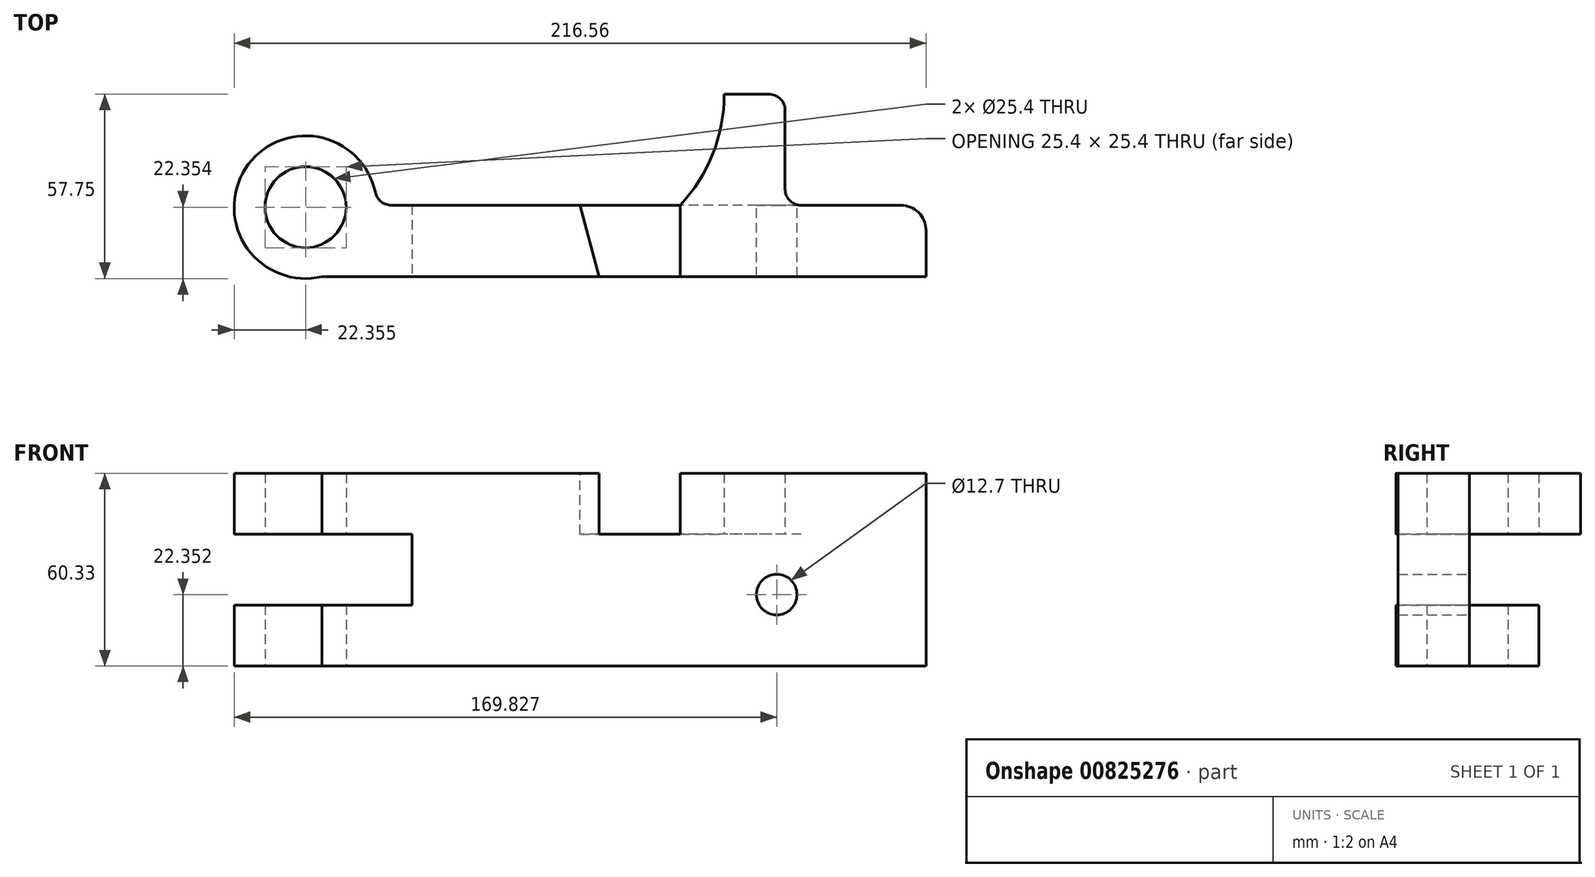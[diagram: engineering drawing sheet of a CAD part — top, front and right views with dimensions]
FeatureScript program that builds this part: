
annotation { "Feature Type Name" : "Feature", "Feature Type Description" : "" }
export const myFeature = defineFeature(function(context is Context, id is Id, definition is map)
    precondition{}
    {
        {
            var Q0;
            Q0=qCreatedBy(makeId("Top.planeOp"),FACE);
            var sketch = newSketch(context, id + "F0", { "sketchPlane" : qUnion([Q0])});
            skLineSegment(sketch, "E0", {"start": v(-131.04, -67.31) * mm, "end": v(58.03, -67.31) * mm});
            skArc(sketch, "E1", {"start": v(-113.83, -44.96) * mm, "mid": v(-153.89, -31.92) * mm, "end": v(-131.04, -67.31) * mm});
            skCircle(sketch, "E2", {"center": v(-136.18, -45.56) * mm, "radius": 12.7 * mm});
            skLineSegment(sketch, "E3", {"start": v(-18.93, -67.31) * mm, "end": v(-44.33, -67.31) * mm});
            skLineSegment(sketch, "E4", {"start": v(-113.83, -44.96) * mm, "end": v(58.03, -44.96) * mm});
            skLineSegment(sketch, "E5", {"start": v(58.03, -44.96) * mm, "end": v(58.03, -67.31) * mm});
            skLineSegment(sketch, "E6", {"start": v(-44.33, -67.31) * mm, "end": v(-50.32, -44.96) * mm});
            skLineSegment(sketch, "E7", {"start": v(-50.32, -44.96) * mm, "end": v(-18.93, -44.96) * mm});
            skLineSegment(sketch, "E8", {"start": v(-18.93, -44.96) * mm, "end": v(-18.93, -67.31) * mm});
            skLineSegment(sketch, "E9", {"start": v(13.91, -44.96) * mm, "end": v(13.91, -10.16) * mm});
            skLineSegment(sketch, "E10", {"start": v(13.91, -10.16) * mm, "end": v(-5.14, -10.16) * mm});
            skArc(sketch, "E11", {"start": v(-18.93, -44.96) * mm, "mid": v(-8.71, -28.88) * mm, "end": v(-5.14, -10.16) * mm});
            skSolve(sketch);
        }
        {
            var Q0;
            {var subQ0=sQuery(id+"F0.wireOp",EDGE,"E1");Q0=makeQuery(id+"F0.imprint","IMPRINT",FACE,{"disambiguationData":[TD([[makeQuery(id+"F0.imprint","IMPRINT",EDGE,{"derivedFrom":subQ0}),1.0]])]});}
            var Q1;
            {var subQ2=sQuery(id+"F0.wireOp",EDGE,"E6");Q1=makeQuery(id+"F0.imprint","IMPRINT",FACE,{"disambiguationData":[TD([[makeQuery(id+"F0.imprint","IMPRINT",EDGE,{"derivedFrom":subQ2}),-1.0]])]});}
            var Q2;
            {var subQ0=sQuery(id+"F0.wireOp",EDGE,"E5");Q2=makeQuery(id+"F0.imprint","IMPRINT",FACE,{"disambiguationData":[TD([[makeQuery(id+"F0.imprint","IMPRINT",EDGE,{"derivedFrom":subQ0}),-1.0]])]});}
            var Q3;
            {var subQ2=sQuery(id+"F0.wireOp",EDGE,"E9");Q3=makeQuery(id+"F0.imprint","IMPRINT",FACE,{"disambiguationData":[TD([[makeQuery(id+"F0.imprint","IMPRINT",EDGE,{"derivedFrom":subQ2}),1.0]])]});}
            extrude(context, id + "F1", {"entities" : qUnion([Q0, Q1, Q2, Q3]), "depth" : 60.32 * mm, "offsetDistance" : 25.4 * mm});
        }
        {
            var Q0;
            Q0=makeQuery(id+"F1.opExtrude","SWEPT_EDGE",EDGE,{"disambiguationData":[OSD([sQuery(id+"F0.wireOp",EDGE,"E9"),sQuery(id+"F0.wireOp",EDGE,"E10")])]});
            fillet(context, id + "F2", {"entities" : qUnion([Q0]), "radius" : 5.08 * mm, "tangentPropagation" : true, "allowEdgeOverflow" : false});
        }
        {
            var Q0;
            Q0=makeQuery(id+"F1.opExtrude","SWEPT_EDGE",EDGE,{"disambiguationData":[OSD([sQuery(id+"F0.wireOp",EDGE,"E4"),sQuery(id+"F0.wireOp",EDGE,"E5")])]});
            fillet(context, id + "F3", {"entities" : qUnion([Q0]), "radius" : 7.87 * mm, "tangentPropagation" : true, "allowEdgeOverflow" : false});
        }
        {
            var Q0;
            Q0=makeQuery(id+"F1.opExtrude","CAP_FACE",FACE,{"disambiguationData":[OSD([sQuery(id+"F0.wireOp",EDGE,"E0"),sQuery(id+"F0.wireOp",EDGE,"E1"),sQuery(id+"F0.wireOp",EDGE,"E2"),sQuery(id+"F0.wireOp",EDGE,"E4"),sQuery(id+"F0.wireOp",EDGE,"E5"),sQuery(id+"F0.wireOp",EDGE,"E9"),sQuery(id+"F0.wireOp",EDGE,"E10"),sQuery(id+"F0.wireOp",EDGE,"E11")])],"isStart":false});
            var sketch = newSketch(context, id + "F4", { "sketchPlane" : qUnion([Q0])});
            skLineSegment(sketch, "E12", {"start": v(-18.93, -44.96) * mm, "end": v(-18.93, -67.31) * mm});
            skLineSegment(sketch, "E13", {"start": v(-18.93, -67.31) * mm, "end": v(-44.33, -67.31) * mm});
            skLineSegment(sketch, "E14", {"start": v(-44.33, -67.31) * mm, "end": v(-50.32, -44.96) * mm});
            skLineSegment(sketch, "E15", {"start": v(-50.32, -44.96) * mm, "end": v(-18.93, -44.96) * mm});
            skCircle(sketch, "E16", {"center": v(-136.18, -45.56) * mm, "radius": 12.7 * mm});
            skSolve(sketch);
        }
        {
            var Q0;
            Q0=makeQuery(id+"F4.imprint","IMPRINT",FACE,{"disambiguationData":[TD([[makeQuery(id+"F4.imprint","IMPRINT",EDGE,{"derivedFrom":sQuery(id+"F4.wireOp",EDGE,"E12")}),-1.0]])]});
            extrude(context, id + "F5", {"entities" : qUnion([Q0]), "operationType" : NewBodyOperationType.REMOVE, "oppositeDirection" : true, "depth" : 19.05 * mm, "offsetDistance" : 25.4 * mm});
        }
        {
            var Q0;
            Q0=makeQuery(id+"F1.opExtrude","CAP_FACE",FACE,{"disambiguationData":[OSD([sQuery(id+"F0.wireOp",EDGE,"E0"),sQuery(id+"F0.wireOp",EDGE,"E1"),sQuery(id+"F0.wireOp",EDGE,"E2"),sQuery(id+"F0.wireOp",EDGE,"E4"),sQuery(id+"F0.wireOp",EDGE,"E5"),sQuery(id+"F0.wireOp",EDGE,"E9"),sQuery(id+"F0.wireOp",EDGE,"E10"),sQuery(id+"F0.wireOp",EDGE,"E11")])],"isStart":true});
            var sketch = newSketch(context, id + "F6", { "sketchPlane" : qUnion([Q0])});
            skLineSegment(sketch, "E17", {"start": v(13.91, 44.96) * mm, "end": v(-18.93, 44.96) * mm});
            skSolve(sketch);
        }
        {
            var Q0;
            Q0=makeQuery(id+"F6.imprint","IMPRINT",FACE,{"disambiguationData":[TD([[makeQuery(id+"F6.imprint","IMPRINT",EDGE,{"derivedFrom":sQuery(id+"F6.wireOp",EDGE,"E17")}),1.0]])]});
            extrude(context, id + "F7", {"entities" : qUnion([Q0]), "operationType" : NewBodyOperationType.REMOVE, "oppositeDirection" : true, "depth" : 41.27 * mm, "offsetDistance" : 25.4 * mm});
        }
        {
            var Q0;
            {var subQ0=sQuery(id+"F0.wireOp",EDGE,"E4");var subQ1=makeQuery(id+"F0.imprint","INTERSECT",VERTEX,{"derivedFrom":[subQ0,sQuery(id+"F0.wireOp",EDGE,"E6")]});Q0=makeQuery(id+"F7.boolean.opBoolean","MERGE",FACE,{"derivedFrom":[makeQuery(id+"F1.opExtrude","SWEPT_FACE",FACE,{"disambiguationData":[OSD([subQ0]),TDD([makeQuery(id+"F0.imprint","IMPRINT",EDGE,{"disambiguationData":[TD([[makeQuery(id+"F0.imprint","INTERSECT",VERTEX,{"derivedFrom":[subQ0,sQuery(id+"F0.wireOp",EDGE,"E5")]}),1.0]])],"derivedFrom":subQ0})])]}),makeQuery(id+"F1.opExtrude","SWEPT_FACE",FACE,{"disambiguationData":[OSD([subQ0]),TDD([makeQuery(id+"F0.imprint","IMPRINT",EDGE,{"disambiguationData":[TD([[makeQuery(id+"F0.imprint","INTERSECT",VERTEX,{"derivedFrom":[sQuery(id+"F0.wireOp",EDGE,"E1"),subQ0]}),-1.0]])],"derivedFrom":subQ0}),makeQuery(id+"F0.imprint","IMPRINT",EDGE,{"disambiguationData":[TD([[subQ1,-1.0]])],"derivedFrom":subQ0})])]})],"fromTools":[makeQuery(id+"F7.opExtrude","SWEPT_FACE",FACE,{"disambiguationData":[OSD([sQuery(id+"F6.wireOp",EDGE,"E17")])]})]});}
            var sketch = newSketch(context, id + "F8", { "sketchPlane" : qUnion([Q0])});
            skCircle(sketch, "E18", {"center": v(-11.3, 22.35) * mm, "radius": 6.35 * mm});
            skSolve(sketch);
        }
        {
            var Q0;
            Q0=makeQuery(id+"F8.imprint","IMPRINT",FACE,{"disambiguationData":[TD([[makeQuery(id+"F8.imprint","IMPRINT",EDGE,{"derivedFrom":sQuery(id+"F8.wireOp",EDGE,"E18")}),1.0]])]});
            extrude(context, id + "F9", {"entities" : qUnion([Q0]), "operationType" : NewBodyOperationType.REMOVE, "endBound" : BoundingType.THROUGH_ALL, "oppositeDirection" : true, "depth" : 25.4 * mm, "offsetDistance" : 25.4 * mm});
        }
        {
            var Q0;
            Q0=makeQuery(id+"F1.opExtrude","SWEPT_EDGE",EDGE,{"disambiguationData":[OSD([sQuery(id+"F0.wireOp",EDGE,"E4"),sQuery(id+"F0.wireOp",EDGE,"E9")])]});
            fillet(context, id + "F10", {"entities" : qUnion([Q0]), "radius" : 5.08 * mm, "tangentPropagation" : true, "allowEdgeOverflow" : false});
        }
        {
            var Q0;
            Q0=makeQuery(id+"F1.opExtrude","SWEPT_EDGE",EDGE,{"disambiguationData":[OSD([sQuery(id+"F0.wireOp",EDGE,"E1"),sQuery(id+"F0.wireOp",EDGE,"E4")])]});
            fillet(context, id + "F11", {"entities" : qUnion([Q0]), "radius" : 5.08 * mm, "tangentPropagation" : true, "allowEdgeOverflow" : false});
        }
        {
            var Q0;
            Q0=qCreatedBy(makeId("Right.planeOp"),FACE);
            cPlane(context, id + "F12", {"entities" : qUnion([Q0]), "cplaneType" : CPlaneType.OFFSET, "offset" : 160.02 * mm, "oppositeDirection" : true, "width" : 152.4 * mm, "height" : 152.4 * mm});
        }
        {
            var Q0;
            Q0=qCreatedBy(id+"F12.planeOp",FACE);
            var sketch = newSketch(context, id + "F13", { "sketchPlane" : qUnion([Q0])});
            skLineSegment(sketch, "E19.bottom", {"start": v(-13.57, 19.05) * mm, "end": v(-77.39, 19.05) * mm});
            skLineSegment(sketch, "E19.top", {"start": v(-13.57, 41.28) * mm, "end": v(-77.39, 41.27) * mm});
            skLineSegment(sketch, "E19.left", {"start": v(-13.57, 19.05) * mm, "end": v(-13.57, 41.28) * mm});
            skLineSegment(sketch, "E19.right", {"start": v(-77.39, 19.05) * mm, "end": v(-77.39, 41.27) * mm});
            skSolve(sketch);
        }
        {
            var Q0;
            Q0=makeQuery(id+"F13.imprint","IMPRINT",FACE,{"disambiguationData":[TD([[makeQuery(id+"F13.imprint","IMPRINT",EDGE,{"derivedFrom":sQuery(id+"F13.wireOp",EDGE,"E19.bottom")}),-1.0]])]});
            extrude(context, id + "F14", {"entities" : qUnion([Q0]), "operationType" : NewBodyOperationType.REMOVE, "depth" : 57.15 * mm, "offsetDistance" : 25.4 * mm});
        }
    });
